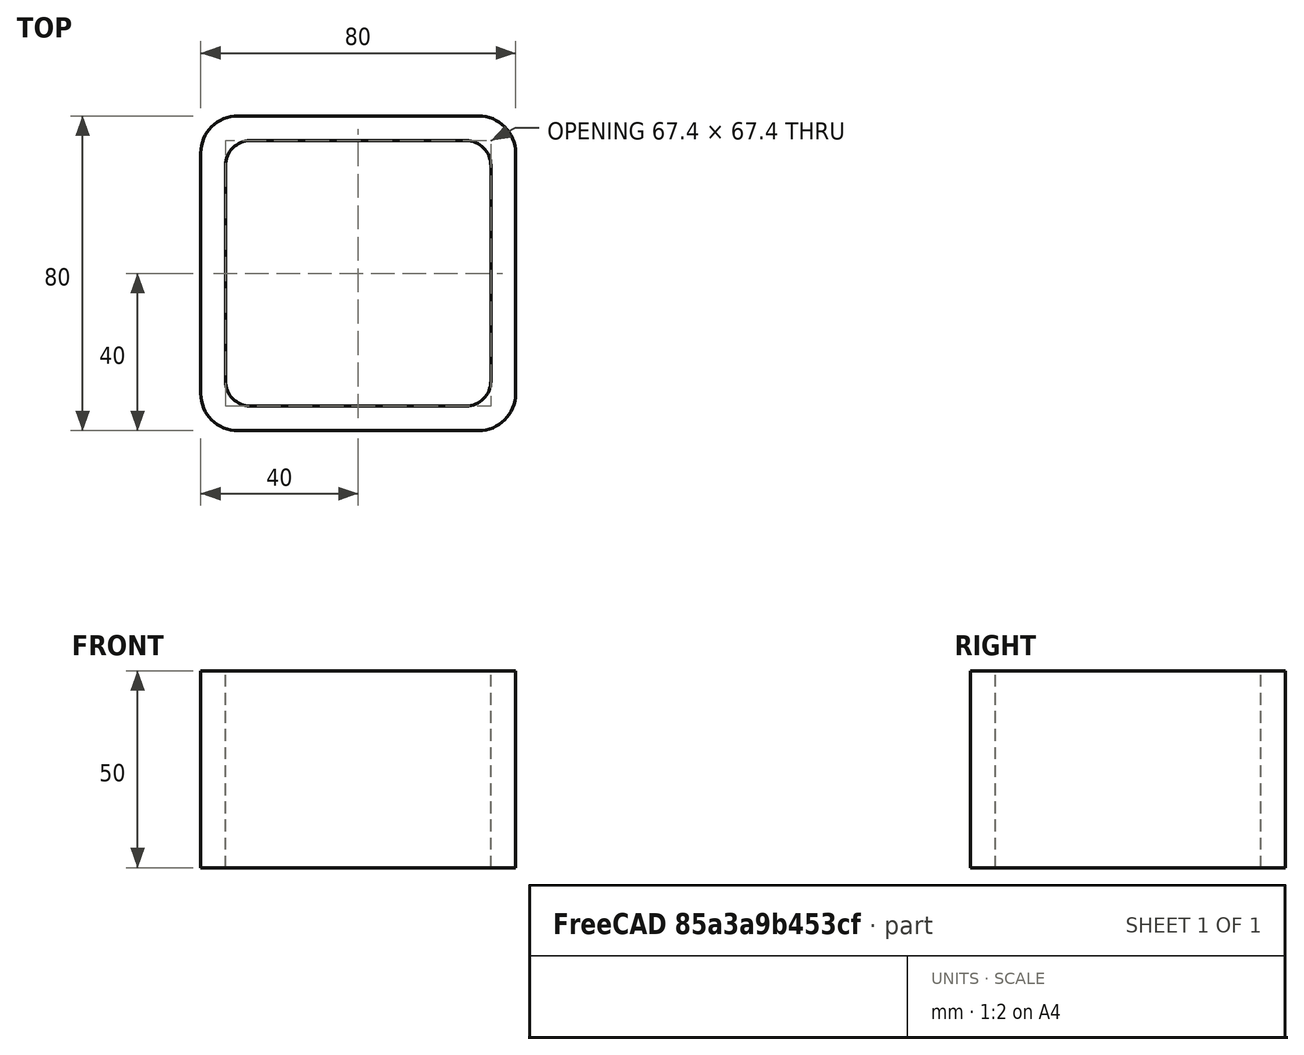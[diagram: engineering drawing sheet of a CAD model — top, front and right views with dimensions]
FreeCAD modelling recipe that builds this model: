
FCSTD DOCUMENT  (FreeCAD 0.15R4671 (Git))
Label: Square hollow section 80x80x6.3 EN10219 S235JRH
License: All rights reserved
LicenseURL: http://en.wikipedia.org/wiki/All_rights_reserved
objects: Sketcher::SketchObject×1, Part::Extrusion×1
note: 2 computed .brp shape members not serialized (recipe doc carries the construction recipe); baked Part::Feature solids carry a one-line shape summary decoded from their .brp

FEATURE [Sketcher::SketchObject] Sketch
  sketch-geometry (16):
    g0: LineSegment StartX=-27.4 StartY=33.7 StartZ=0 EndX=27.4 EndY=33.7 EndZ=0
    g1: LineSegment StartX=33.7 StartY=27.4 StartZ=0 EndX=33.7 EndY=-27.4 EndZ=0
    g2: LineSegment StartX=27.4 StartY=-33.7 StartZ=0 EndX=-27.4 EndY=-33.7 EndZ=0
    g3: LineSegment StartX=-33.7 StartY=-27.4 StartZ=0 EndX=-33.7 EndY=27.4 EndZ=0
    g4: LineSegment StartX=-30.55 StartY=40 StartZ=0 EndX=30.55 EndY=40 EndZ=0
    g5: LineSegment StartX=40 StartY=30.55 StartZ=0 EndX=40 EndY=-30.55 EndZ=0
    g6: LineSegment StartX=30.55 StartY=-40 StartZ=0 EndX=-30.55 EndY=-40 EndZ=0
    g7: LineSegment StartX=-40 StartY=-30.55 StartZ=0 EndX=-40 EndY=30.55 EndZ=0
    g8: ArcOfCircle CenterX=-27.4 CenterY=27.4 CenterZ=0 NormalX=0 NormalY=0 NormalZ=1 Radius=6.3 StartAngle=1.5708 EndAngle=3.14159
    g9: ArcOfCircle CenterX=27.4 CenterY=27.4 CenterZ=0 NormalX=0 NormalY=0 NormalZ=1 Radius=6.3 StartAngle=0 EndAngle=1.5708
    g10: ArcOfCircle CenterX=27.4 CenterY=-27.4 CenterZ=0 NormalX=0 NormalY=0 NormalZ=1 Radius=6.3 StartAngle=4.71239 EndAngle=6.28319
    g11: ArcOfCircle CenterX=-27.4 CenterY=-27.4 CenterZ=0 NormalX=0 NormalY=0 NormalZ=1 Radius=6.3 StartAngle=3.14159 EndAngle=4.71239
    g12: ArcOfCircle CenterX=30.55 CenterY=30.55 CenterZ=0 NormalX=0 NormalY=0 NormalZ=1 Radius=9.45 StartAngle=0 EndAngle=1.5708
    g13: ArcOfCircle CenterX=30.55 CenterY=-30.55 CenterZ=0 NormalX=0 NormalY=0 NormalZ=1 Radius=9.45 StartAngle=4.71239 EndAngle=6.28319
    g14: ArcOfCircle CenterX=-30.55 CenterY=-30.55 CenterZ=0 NormalX=0 NormalY=0 NormalZ=1 Radius=9.45 StartAngle=3.14159 EndAngle=4.71239
    g15: ArcOfCircle CenterX=-30.55 CenterY=30.55 CenterZ=0 NormalX=0 NormalY=0 NormalZ=1 Radius=9.45 StartAngle=1.5708 EndAngle=3.14159
  constraints (36):
    c: Horizontal(g2)
    c: Vertical(g3)
    c: Horizontal(g6)
    c: Vertical(g7)
    c: Tangent(g3,g8) = 1.5708
    c: Tangent(g0,g8) = 1.5708
    c: Tangent(g0,g9) = 1.5708
    c: Tangent(g1,g9) = 1.5708
    c: Tangent(g1,g10) = 1.5708
    c: Tangent(g2,g10) = 1.5708
    c: Tangent(g2,g11) = 1.5708
    c: Tangent(g3,g11) = 1.5708
    c: Tangent(g4,g12) = 1.5708
    c: Tangent(g5,g12) = 1.5708
    c: Tangent(g5,g13) = 1.5708
    c: Tangent(g6,g13) = 1.5708
    c: Tangent(g6,g14) = 1.5708
    c: Tangent(g7,g14) = 1.5708
    c: Tangent(g7,g15) = 1.5708
    c: Tangent(g4,g15) = 1.5708
    c: Equal(g9,g8)
    c: Equal(g9,g11)
    c: Equal(g9,g10)
    c: Equal(g12,g15)
    c: Equal(g12,g14)
    c: Equal(g12,g13)
    c: Symmetric(g4,g6,g-1)
    c: Symmetric(g7,g5,g-2)
    c: DistanceY(g4,g6) = -80
    c: DistanceX(g7,g5) = 80
    c: Symmetric(g3,g1,g-2)
    c: Symmetric(g0,g2,g-1)
    c: DistanceY(g0,g4) = 6.3
    c: DistanceX(g5,g1) = -6.3
    c: Radius(g9) = 6.3
    c: Radius(g12) = 9.45
FEATURE [Part::Extrusion] Extrude  label="Square hollow section 80x80x6.3 EN10219 S235JRH"
  Base = -> Sketch
  Dir = (0,0,50)
  Solid = true
